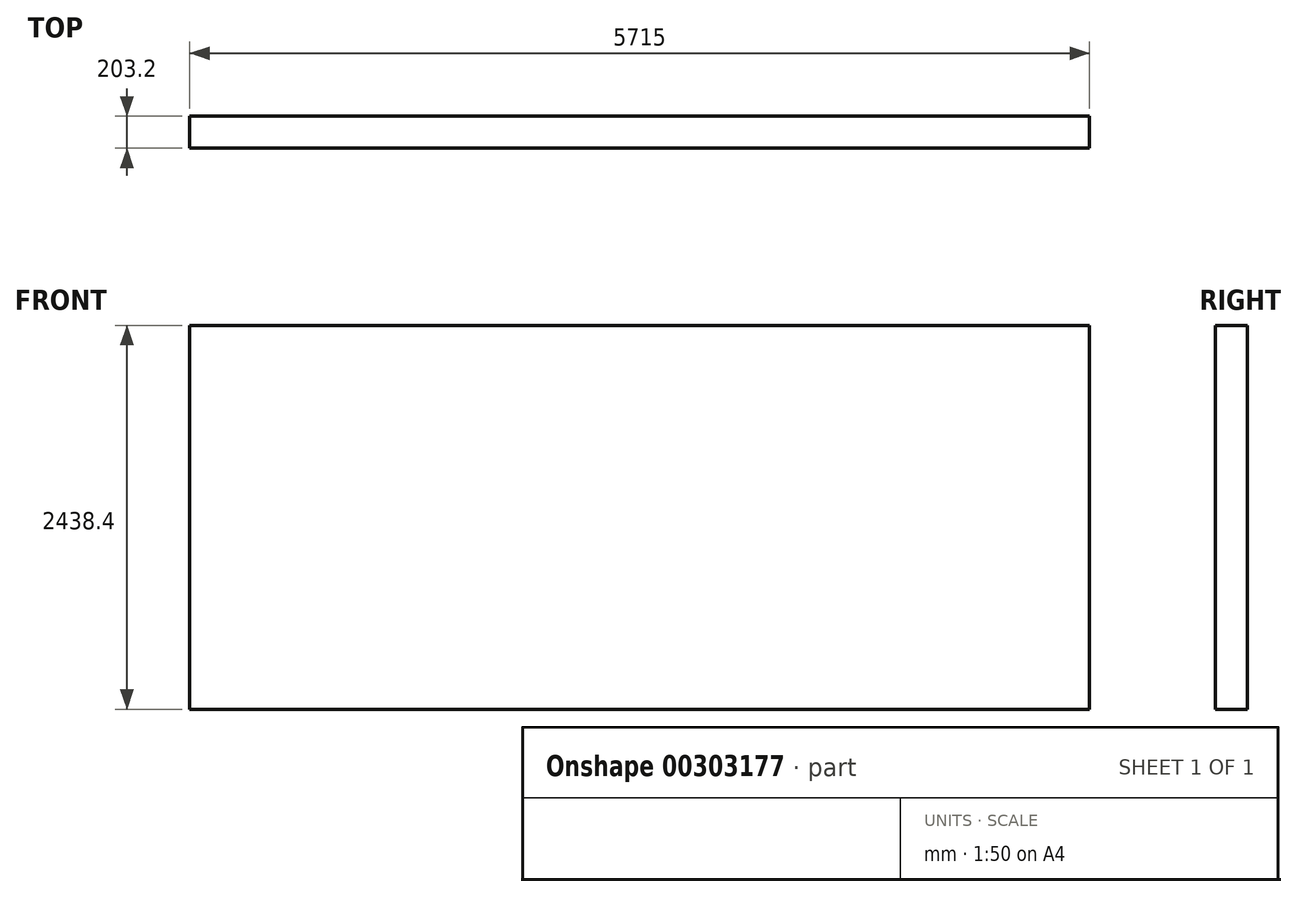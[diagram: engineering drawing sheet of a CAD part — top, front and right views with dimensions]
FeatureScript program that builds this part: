
annotation { "Feature Type Name" : "Feature", "Feature Type Description" : "" }
export const myFeature = defineFeature(function(context is Context, id is Id, definition is map)
    precondition{}
    {
        {
            var Q0;
            Q0=qCreatedBy(makeId("Top.planeOp"),FACE);
            var sketch = newSketch(context, id + "F0", { "sketchPlane" : qUnion([Q0])});
            skLineSegment(sketch, "E0.bottom", {"start": v(2857.5, -101.6) * mm, "end": v(-2857.5, -101.6) * mm});
            skLineSegment(sketch, "E0.top", {"start": v(2857.5, 101.6) * mm, "end": v(-2857.5, 101.6) * mm});
            skLineSegment(sketch, "E0.left", {"start": v(2857.5, -101.6) * mm, "end": v(2857.5, 101.6) * mm});
            skLineSegment(sketch, "E0.right", {"start": v(-2857.5, -101.6) * mm, "end": v(-2857.5, 101.6) * mm});
            skPoint(sketch, "E0.middle", {"position": v(0, 0) * mm});
            skSolve(sketch);
        }
        {
            var Q0;
            Q0=makeQuery(id+"F0.imprint","IMPRINT",FACE,{"disambiguationData":[TD([[makeQuery(id+"F0.imprint","IMPRINT",EDGE,{"derivedFrom":sQuery(id+"F0.wireOp",EDGE,"E0.bottom")}),-1.0]])]});
            extrude(context, id + "F1", {"entities" : qUnion([Q0]), "depth" : 2438.4 * mm});
        }
    });
